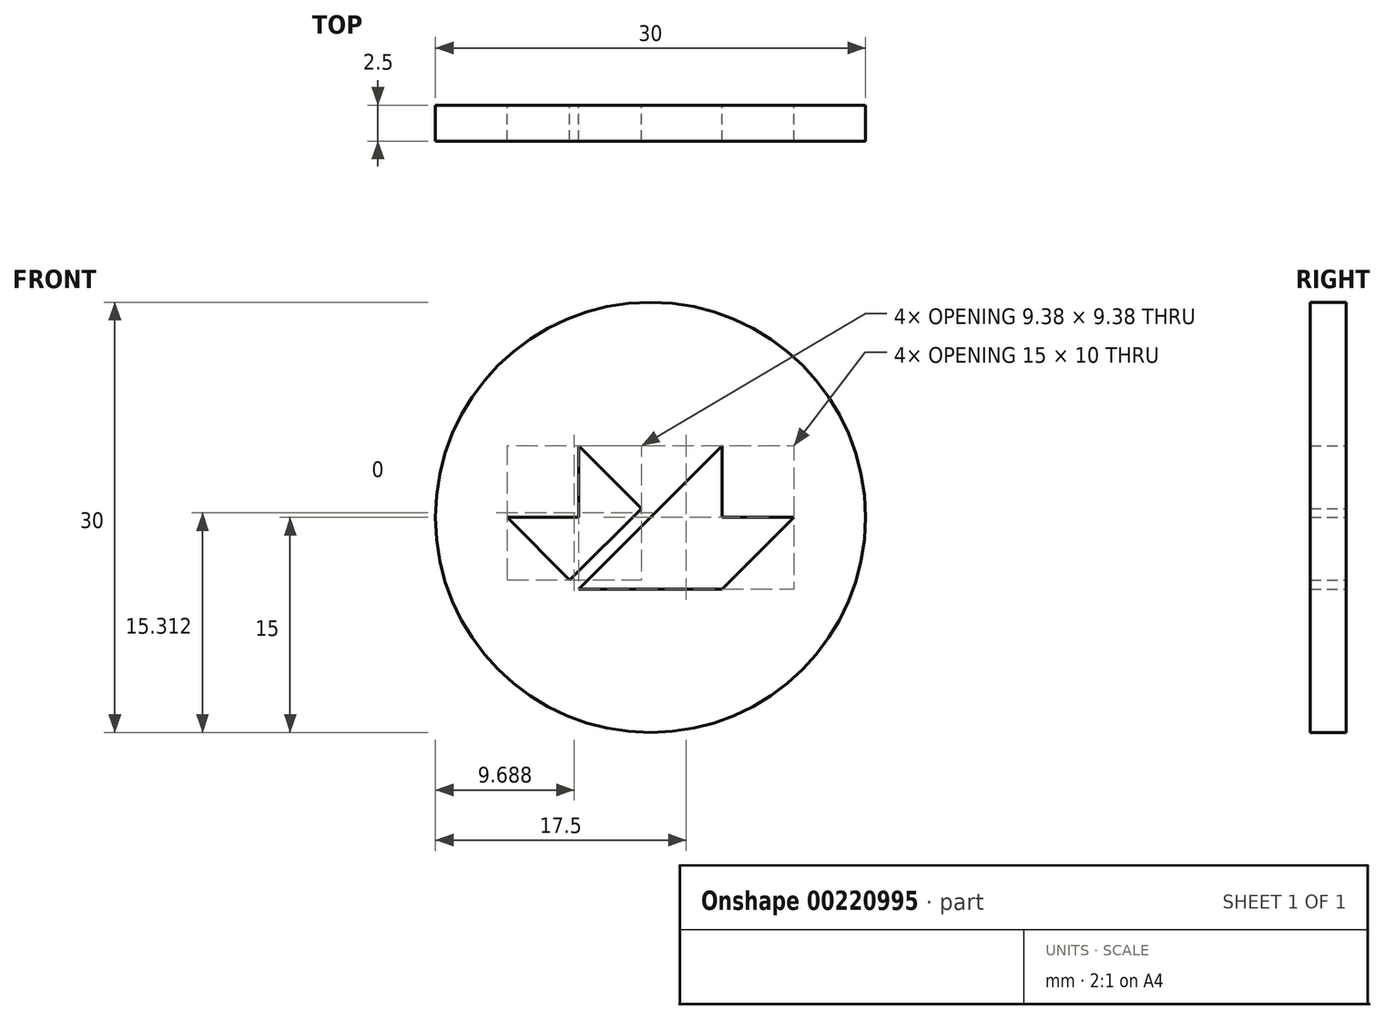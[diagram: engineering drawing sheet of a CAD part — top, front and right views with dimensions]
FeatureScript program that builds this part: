
annotation { "Feature Type Name" : "Feature", "Feature Type Description" : "" }
export const myFeature = defineFeature(function(context is Context, id is Id, definition is map)
    precondition{}
    {
        {
            var Q0;
            Q0=qCreatedBy(makeId("Front.planeOp"),FACE);
            var sketch = newSketch(context, id + "F0", { "sketchPlane" : qUnion([Q0])});
            skLineSegment(sketch, "E0.bottom", {"start": v(0, 0) * mm, "end": v(10, 0) * mm});
            skLineSegment(sketch, "E0.top", {"start": v(0, 10) * mm, "end": v(10, 10) * mm});
            skLineSegment(sketch, "E0.left", {"start": v(0, 0) * mm, "end": v(0, 10) * mm});
            skLineSegment(sketch, "E0.right", {"start": v(10, 0) * mm, "end": v(10, 10) * mm});
            skLineSegment(sketch, "E1", {"start": v(10, 10) * mm, "end": v(20, 10) * mm});
            skLineSegment(sketch, "E2", {"start": v(20, 10) * mm, "end": v(20, 0) * mm});
            skLineSegment(sketch, "E3", {"start": v(20, 0) * mm, "end": v(10, 0) * mm});
            skLineSegment(sketch, "E4", {"start": v(0, 5) * mm, "end": v(10, 5) * mm});
            skLineSegment(sketch, "E5", {"start": v(10, 5) * mm, "end": v(20, 5) * mm});
            skLineSegment(sketch, "E6", {"start": v(5, 10) * mm, "end": v(5, 0) * mm});
            skLineSegment(sketch, "E7", {"start": v(15, 10) * mm, "end": v(15, 0) * mm});
            skLineSegment(sketch, "E8", {"start": v(20, 0) * mm, "end": v(10, 10) * mm});
            skLineSegment(sketch, "E9", {"start": v(10, 10) * mm, "end": v(0, 0) * mm});
            skLineSegment(sketch, "E10", {"start": v(0, 10) * mm, "end": v(10, 0) * mm});
            skLineSegment(sketch, "E11", {"start": v(10, 0) * mm, "end": v(20, 10) * mm});
            skLineSegment(sketch, "E12", {"start": v(20, 5) * mm, "end": v(15, 10) * mm});
            skLineSegment(sketch, "E13", {"start": v(15, 10) * mm, "end": v(5, 0) * mm});
            skLineSegment(sketch, "E14", {"start": v(5, 0) * mm, "end": v(0, 5) * mm});
            skLineSegment(sketch, "E15", {"start": v(0, 5) * mm, "end": v(5, 10) * mm});
            skLineSegment(sketch, "E16", {"start": v(5, 10) * mm, "end": v(15, 0) * mm});
            skLineSegment(sketch, "E17", {"start": v(15, 0) * mm, "end": v(20, 5) * mm});
            skCircle(sketch, "E18", {"center": v(10, 5) * mm, "radius": 15 * mm});
            skLineSegment(sketch, "E19", {"start": v(20, 5) * mm, "end": v(25, 5) * mm});
            skLineSegment(sketch, "E20", {"start": v(20, 10) * mm, "end": v(25, 5) * mm});
            skLineSegment(sketch, "E21", {"start": v(20, 0) * mm, "end": v(25, 5) * mm});
            skLineSegment(sketch, "E22", {"start": v(7.5, 2.5) * mm, "end": v(7.5, 5) * mm});
            skSolve(sketch);
        }
        {
            var Q0;
            Q0=qCreatedBy(makeId("Front.planeOp"),FACE);
            var sketch = newSketch(context, id + "F1", { "sketchPlane" : qUnion([Q0])});
            skLineSegment(sketch, "E23", {"start": v(5, 0) * mm, "end": v(15, 10) * mm});
            skLineSegment(sketch, "E24", {"start": v(15, 10) * mm, "end": v(15, 5) * mm});
            skLineSegment(sketch, "E25", {"start": v(15, 5) * mm, "end": v(20, 5) * mm});
            skLineSegment(sketch, "E26", {"start": v(20, 5) * mm, "end": v(15, 0) * mm});
            skLineSegment(sketch, "E27", {"start": v(15, 0) * mm, "end": v(5, 0) * mm});
            skLineSegment(sketch, "E28", {"start": v(0, 5) * mm, "end": v(4.38, 0.63) * mm});
            skLineSegment(sketch, "E29", {"start": v(4.37, 0.63) * mm, "end": v(9.38, 5.63) * mm});
            skLineSegment(sketch, "E30", {"start": v(9.38, 5.63) * mm, "end": v(5, 10) * mm});
            skLineSegment(sketch, "E31", {"start": v(5, 10) * mm, "end": v(5, 5) * mm});
            skLineSegment(sketch, "E32", {"start": v(5, 5) * mm, "end": v(0, 5) * mm});
            skCircle(sketch, "E33.0", {"center": v(10, 5) * mm, "radius": 15 * mm});
            skSolve(sketch);
        }
        {
            var Q0;
            Q0=makeQuery(id+"F1.imprint","IMPRINT",FACE,{"disambiguationData":[TD([[makeQuery(id+"F1.imprint","IMPRINT",EDGE,{"derivedFrom":sQuery(id+"F1.wireOp",EDGE,"E23")}),1.0]])]});
            extrude(context, id + "F2", {"entities" : qUnion([Q0]), "depth" : 2.5 * mm});
        }
    });
